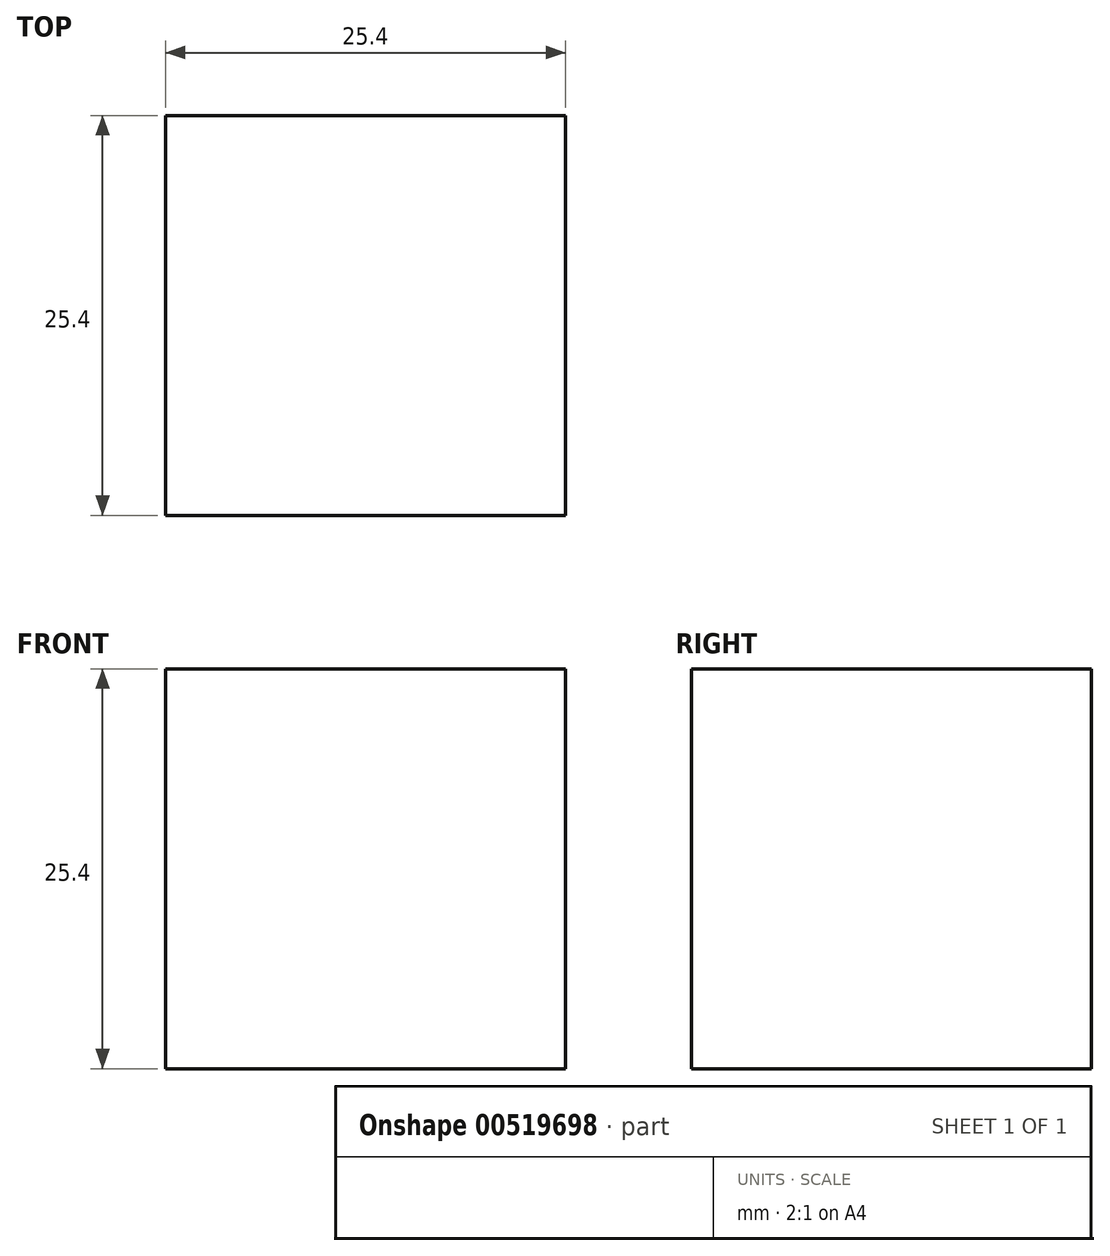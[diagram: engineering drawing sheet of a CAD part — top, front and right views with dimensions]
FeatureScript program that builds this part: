
annotation { "Feature Type Name" : "Feature", "Feature Type Description" : "" }
export const myFeature = defineFeature(function(context is Context, id is Id, definition is map)
    precondition{}
    {
        {
            var Q0;
            Q0=qCreatedBy(makeId("Top.planeOp"),FACE);
            var sketch = newSketch(context, id + "F0", { "sketchPlane" : qUnion([Q0])});
            skLineSegment(sketch, "E0.bottom", {"start": v(0, 0) * mm, "end": v(-25.4, 0) * mm});
            skLineSegment(sketch, "E0.top", {"start": v(0, -25.4) * mm, "end": v(-25.4, -25.4) * mm});
            skLineSegment(sketch, "E0.left", {"start": v(0, 0) * mm, "end": v(0, -25.4) * mm});
            skLineSegment(sketch, "E0.right", {"start": v(-25.4, 0) * mm, "end": v(-25.4, -25.4) * mm});
            skSolve(sketch);
        }
        {
            var Q0;
            Q0 = qSketchRegion(id + "F0", true);
            extrude(context, id + "F1", {"entities" : qUnion([Q0]), "flatOperationType" : FlatOperationType.REMOVE, "depth" : 25.4 * mm, "offsetDistance" : 25.4 * mm, "domain" : OperationDomain.MODEL});
        }
        {
            var Q0;
            Q0=makeQuery(id+"F1.opExtrude","SWEPT_BODY",BODY,{"disambiguationData":[OSD([sQuery(id+"F0.wireOp",EDGE,"E0.bottom"),sQuery(id+"F0.wireOp",EDGE,"E0.top"),sQuery(id+"F0.wireOp",EDGE,"E0.left"),sQuery(id+"F0.wireOp",EDGE,"E0.right")])]});
            transform(context, id + "F2", {"entities" : qUnion([Q0]), "transformType" : TransformType.TRANSLATION_3D, "dx" : 0 * mm, "dy" : 0 * mm, "dz" : 0 * mm, "makeCopy" : true});
        }
    });
